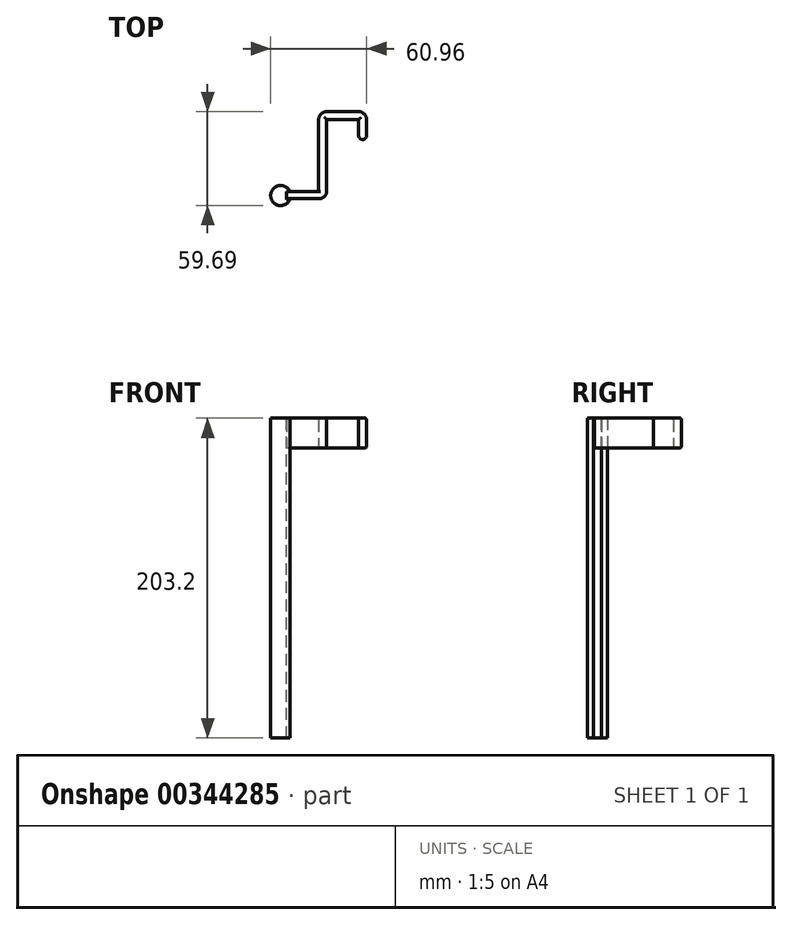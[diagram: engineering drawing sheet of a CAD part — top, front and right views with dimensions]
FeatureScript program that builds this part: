
annotation { "Feature Type Name" : "Feature", "Feature Type Description" : "" }
export const myFeature = defineFeature(function(context is Context, id is Id, definition is map)
    precondition{}
    {
        {
            var Q0;
            Q0=qCreatedBy(makeId("Top.planeOp"),FACE);
            var sketch = newSketch(context, id + "F0", { "sketchPlane" : qUnion([Q0])});
            skCircle(sketch, "E0", {"center": v(-37.51, 29.2) * mm, "radius": 6.35 * mm});
            skSolve(sketch);
        }
        {
            var Q0;
            Q0 = qSketchRegion(id + "F0", true);
            extrude(context, id + "F1", {"entities" : qUnion([Q0]), "depth" : 203.2 * mm});
        }
        {
            var Q0;
            Q0=makeQuery(id+"F1.opExtrude","CAP_FACE",FACE,{"disambiguationData":[OSD([sQuery(id+"F0.wireOp",EDGE,"E0")])],"isStart":false});
            var sketch = newSketch(context, id + "F2", { "sketchPlane" : qUnion([Q0])});
            skLineSegment(sketch, "E1", {"start": v(-37.51, 29.2) * mm, "end": v(-31.16, 29.2) * mm});
            skLineSegment(sketch, "E2", {"start": v(-31.16, 29.2) * mm, "end": v(-31.16, 31.74) * mm});
            skLineSegment(sketch, "E3", {"start": v(-31.16, 31.74) * mm, "end": v(-33.7, 31.74) * mm});
            skLineSegment(sketch, "E4", {"start": v(-33.7, 31.74) * mm, "end": v(-33.7, 26.66) * mm});
            skLineSegment(sketch, "E5", {"start": v(-33.7, 26.66) * mm, "end": v(-31.16, 26.66) * mm});
            skLineSegment(sketch, "E6", {"start": v(-31.16, 26.66) * mm, "end": v(-31.16, 29.2) * mm});
            skSolve(sketch);
        }
        {
            var Q0;
            Q0 = qSketchRegion(id + "F2", true);
            extrude(context, id + "F3", {"entities" : qUnion([Q0]), "operationType" : NewBodyOperationType.REMOVE, "oppositeDirection" : true, "depth" : 227.84 * mm});
        }
        {
            var Q0;
            Q0=makeQuery(id+"F3.boolean.opBoolean","COPY",FACE,{"derivedFrom":makeQuery(id+"F3.opExtrude","SWEPT_FACE",FACE,{"disambiguationData":[OSD([sQuery(id+"F2.wireOp",EDGE,"E4")])]})});
            var sketch = newSketch(context, id + "F4", { "sketchPlane" : qUnion([Q0])});
            skLineSegment(sketch, "E7.bottom", {"start": v(31.74, 203.2) * mm, "end": v(27.17, 203.2) * mm});
            skLineSegment(sketch, "E7.top", {"start": v(31.74, 184.15) * mm, "end": v(27.17, 184.15) * mm});
            skLineSegment(sketch, "E7.left", {"start": v(31.74, 203.2) * mm, "end": v(31.74, 184.15) * mm});
            skLineSegment(sketch, "E8", {"start": v(27.17, 203.2) * mm, "end": v(27.17, 184.15) * mm});
            skLineSegment(sketch, "E9", {"start": v(27.17, 184.15) * mm, "end": v(31.74, 184.15) * mm});
            skSolve(sketch);
        }
        {
            var Q0;
            Q0 = qSketchRegion(id + "F4", true);
            extrude(context, id + "F5", {"entities" : qUnion([Q0]), "depth" : 25.4 * mm});
        }
        {
            var Q0;
            Q0=makeQuery(id+"F5.opExtrude","SWEPT_FACE",FACE,{"disambiguationData":[OSD([sQuery(id+"F4.wireOp",EDGE,"E7.left")])]});
            var sketch = newSketch(context, id + "F6", { "sketchPlane" : qUnion([Q0])});
            skLineSegment(sketch, "E10", {"start": v(8.3, 203.2) * mm, "end": v(13.38, 203.2) * mm});
            skLineSegment(sketch, "E11", {"start": v(13.38, 203.2) * mm, "end": v(13.38, 184.15) * mm});
            skLineSegment(sketch, "E12", {"start": v(13.38, 184.15) * mm, "end": v(8.3, 184.15) * mm});
            skLineSegment(sketch, "E13", {"start": v(8.3, 184.15) * mm, "end": v(8.3, 203.2) * mm});
            skSolve(sketch);
        }
        {
            var Q0;
            Q0 = qSketchRegion(id + "F6", true);
            extrude(context, id + "F7", {"entities" : qUnion([Q0]), "operationType" : NewBodyOperationType.ADD, "depth" : 50.8 * mm});
        }
        {
            var Q0;
            Q0=makeQuery(id+"F7.boolean.opBoolean","MERGE",FACE,{"derivedFrom":[makeQuery(id+"F5.opExtrude","CAP_FACE",FACE,{"disambiguationData":[OSD([sQuery(id+"F4.wireOp",EDGE,"E7.bottom"),sQuery(id+"F4.wireOp",EDGE,"E7.top"),sQuery(id+"F4.wireOp",EDGE,"E7.left"),sQuery(id+"F4.wireOp",EDGE,"E7.right")])],"isStart":false}),makeQuery(id+"F7.opExtrude","SWEPT_FACE",FACE,{"disambiguationData":[OSD([sQuery(id+"F6.wireOp",EDGE,"E13")])]})]});
            var sketch = newSketch(context, id + "F8", { "sketchPlane" : qUnion([Q0])});
            skLineSegment(sketch, "E14", {"start": v(82.54, 203.2) * mm, "end": v(77.46, 203.2) * mm});
            skLineSegment(sketch, "E15", {"start": v(77.46, 203.2) * mm, "end": v(77.46, 184.15) * mm});
            skLineSegment(sketch, "E16", {"start": v(77.46, 184.15) * mm, "end": v(82.54, 184.15) * mm});
            skLineSegment(sketch, "E17", {"start": v(82.54, 184.15) * mm, "end": v(82.54, 203.2) * mm});
            skSolve(sketch);
        }
        {
            var Q0;
            Q0 = qSketchRegion(id + "F8", true);
            extrude(context, id + "F9", {"entities" : qUnion([Q0]), "operationType" : NewBodyOperationType.ADD, "depth" : 25.4 * mm});
        }
        {
            var Q0;
            Q0=makeQuery(id+"F9.opExtrude","SWEPT_FACE",FACE,{"disambiguationData":[OSD([sQuery(id+"F8.wireOp",EDGE,"E15")])]});
            var sketch = newSketch(context, id + "F10", { "sketchPlane" : qUnion([Q0])});
            skLineSegment(sketch, "E18", {"start": v(17.1, 203.2) * mm, "end": v(12.02, 203.2) * mm});
            skLineSegment(sketch, "E19", {"start": v(12.02, 203.2) * mm, "end": v(12.02, 184.15) * mm});
            skLineSegment(sketch, "E20", {"start": v(12.02, 184.15) * mm, "end": v(17.1, 184.15) * mm});
            skLineSegment(sketch, "E21", {"start": v(17.1, 184.15) * mm, "end": v(17.1, 203.2) * mm});
            skSolve(sketch);
        }
        {
            var Q0;
            Q0 = qSketchRegion(id + "F10", true);
            extrude(context, id + "F11", {"entities" : qUnion([Q0]), "operationType" : NewBodyOperationType.ADD, "depth" : 12.7 * mm});
        }
        {
            var Q0;
            Q0=makeQuery(id+"F5.opExtrude","CAP_EDGE",EDGE,{"disambiguationData":[OSD([sQuery(id+"F4.wireOp",EDGE,"E7.right")])],"isStart":false});
            var Q1;
            Q1=makeQuery(id+"F7.opExtrude","CAP_EDGE",EDGE,{"disambiguationData":[OSD([sQuery(id+"F6.wireOp",EDGE,"E11")])],"isStart":false});
            var Q2;
            Q2=makeQuery(id+"F9.opExtrude","CAP_EDGE",EDGE,{"disambiguationData":[OSD([sQuery(id+"F8.wireOp",EDGE,"E17")])],"isStart":false});
            fillet(context, id + "F12", {"entities" : qUnion([Q0, Q1, Q2]), "radius" : 5.08 * mm, "tangentPropagation" : true, "allowEdgeOverflow" : false});
        }
        {
            var Q0;
            Q0=makeQuery(id+"F11.opExtrude","CAP_EDGE",EDGE,{"disambiguationData":[OSD([sQuery(id+"F10.wireOp",EDGE,"E19")])],"isStart":false});
            var Q1;
            Q1=makeQuery(id+"F11.opExtrude","CAP_EDGE",EDGE,{"disambiguationData":[OSD([sQuery(id+"F10.wireOp",EDGE,"E21")])],"isStart":false});
            fillet(context, id + "F13", {"entities" : qUnion([Q0, Q1]), "radius" : 2.54 * mm, "tangentPropagation" : true, "allowEdgeOverflow" : false});
        }
        {
            var Q0;
            Q0=makeQuery(id+"F5.opExtrude","CAP_EDGE",EDGE,{"disambiguationData":[OSD([sQuery(id+"F4.wireOp",EDGE,"E8")])],"isStart":false});
            fillet(context, id + "F14", {"entities" : qUnion([Q0]), "radius" : 5.08 * mm, "tangentPropagation" : true, "allowEdgeOverflow" : false});
        }
        {
            var Q0;
            Q0=makeQuery(id+"F7.opExtrude","SWEPT_EDGE",EDGE,{"disambiguationData":[OSD([sQuery(id+"F6.wireOp",EDGE,"E10"),sQuery(id+"F6.wireOp",EDGE,"E13")])]});
            var Q1;
            Q1=makeQuery(id+"F9.opExtrude","SWEPT_EDGE",EDGE,{"disambiguationData":[OSD([sQuery(id+"F6.wireOp",EDGE,"E10"),sQuery(id+"F6.wireOp",EDGE,"E13"),sQuery(id+"F8.wireOp",EDGE,"E14"),sQuery(id+"F8.wireOp",EDGE,"E15")])]});
            var Q2;
            Q2=makeQuery(id+"F11.opExtrude","SWEPT_EDGE",EDGE,{"disambiguationData":[OSD([sQuery(id+"F6.wireOp",EDGE,"E10"),sQuery(id+"F6.wireOp",EDGE,"E13"),sQuery(id+"F8.wireOp",EDGE,"E14"),sQuery(id+"F8.wireOp",EDGE,"E15"),sQuery(id+"F10.wireOp",EDGE,"E18"),sQuery(id+"F10.wireOp",EDGE,"E19")])]});
            var Q3;
            Q3=makeQuery(id+"F11.opExtrude","SWEPT_EDGE",EDGE,{"disambiguationData":[OSD([sQuery(id+"F10.wireOp",EDGE,"E20"),sQuery(id+"F10.wireOp",EDGE,"E21")])]});
            var Q4;
            Q4=makeQuery(id+"F12.opFillet","BLEND_EDGE",EDGE,{"blendedFrom":[makeQuery(id+"F9.opExtrude","CAP_EDGE",EDGE,{"disambiguationData":[OSD([sQuery(id+"F8.wireOp",EDGE,"E17")])],"isStart":false}),makeQuery(id+"F9.opExtrude","SWEPT_FACE",FACE,{"disambiguationData":[OSD([sQuery(id+"F8.wireOp",EDGE,"E16")])]})],"blendedInto":[makeQuery(id+"F9.opExtrude","SWEPT_FACE",FACE,{"disambiguationData":[OSD([sQuery(id+"F8.wireOp",EDGE,"E16")])]})]});
            var Q5;
            Q5=makeQuery(id+"F12.opFillet","BLEND_EDGE",EDGE,{"blendedFrom":[makeQuery(id+"F7.opExtrude","CAP_EDGE",EDGE,{"disambiguationData":[OSD([sQuery(id+"F6.wireOp",EDGE,"E11")])],"isStart":false}),makeQuery(id+"F7.opExtrude","SWEPT_FACE",FACE,{"disambiguationData":[OSD([sQuery(id+"F6.wireOp",EDGE,"E12")])]})],"blendedInto":[makeQuery(id+"F7.opExtrude","SWEPT_FACE",FACE,{"disambiguationData":[OSD([sQuery(id+"F6.wireOp",EDGE,"E12")])]})]});
            var Q6;
            Q6=makeQuery(id+"F7.opExtrude","SWEPT_EDGE",EDGE,{"disambiguationData":[OSD([sQuery(id+"F6.wireOp",EDGE,"E12"),sQuery(id+"F6.wireOp",EDGE,"E13")])]});
            var Q7;
            Q7=makeQuery(id+"F9.opExtrude","SWEPT_EDGE",EDGE,{"disambiguationData":[OSD([sQuery(id+"F6.wireOp",EDGE,"E12"),sQuery(id+"F6.wireOp",EDGE,"E13"),sQuery(id+"F8.wireOp",EDGE,"E15"),sQuery(id+"F8.wireOp",EDGE,"E16")])]});
            var Q8;
            Q8=makeQuery(id+"F9.opExtrude","SWEPT_EDGE",EDGE,{"disambiguationData":[OSD([sQuery(id+"F8.wireOp",EDGE,"E14"),sQuery(id+"F8.wireOp",EDGE,"E17")])]});
            var Q9;
            Q9=makeQuery(id+"F12.opFillet","BLEND_EDGE",EDGE,{"blendedFrom":[makeQuery(id+"F7.opExtrude","CAP_EDGE",EDGE,{"disambiguationData":[OSD([sQuery(id+"F6.wireOp",EDGE,"E11")])],"isStart":false}),makeQuery(id+"F7.opExtrude","SWEPT_FACE",FACE,{"disambiguationData":[OSD([sQuery(id+"F6.wireOp",EDGE,"E10")])]})],"blendedInto":[makeQuery(id+"F7.opExtrude","SWEPT_FACE",FACE,{"disambiguationData":[OSD([sQuery(id+"F6.wireOp",EDGE,"E10")])]})]});
            var Q10;
            Q10=makeQuery(id+"F7.opExtrude","SWEPT_EDGE",EDGE,{"disambiguationData":[OSD([sQuery(id+"F4.wireOp",EDGE,"E7.left"),sQuery(id+"F4.wireOp",EDGE,"E7.bottom"),sQuery(id+"F6.wireOp",EDGE,"E10"),sQuery(id+"F6.wireOp",EDGE,"E11")])]});
            var Q11;
            Q11=makeQuery(id+"F5.opExtrude","SWEPT_EDGE",EDGE,{"disambiguationData":[OSD([sQuery(id+"F2.wireOp",EDGE,"E4"),sQuery(id+"F4.wireOp",EDGE,"E7.bottom"),sQuery(id+"F4.wireOp",EDGE,"E8")])]});
            var Q12;
            Q12=makeQuery(id+"F5.opExtrude","SWEPT_EDGE",EDGE,{"disambiguationData":[OSD([sQuery(id+"F4.wireOp",EDGE,"E8"),sQuery(id+"F4.wireOp",EDGE,"E9")])]});
            fillet(context, id + "F15", {"entities" : qUnion([Q0, Q1, Q2, Q3, Q4, Q5, Q6, Q7, Q8, Q9, Q10, Q11, Q12]), "radius" : 1.27 * mm, "tangentPropagation" : true, "allowEdgeOverflow" : false});
        }
    });
